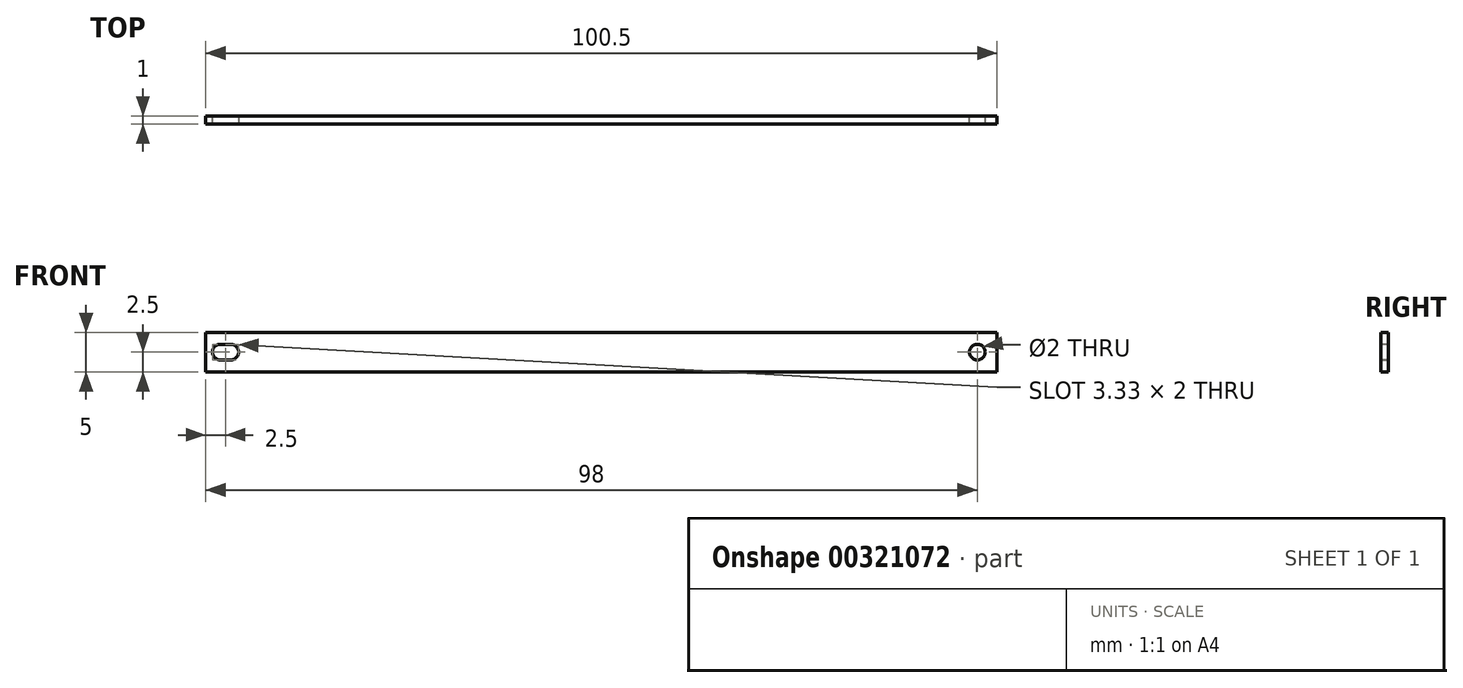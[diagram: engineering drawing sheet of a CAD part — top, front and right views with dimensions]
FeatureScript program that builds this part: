
annotation { "Feature Type Name" : "Feature", "Feature Type Description" : "" }
export const myFeature = defineFeature(function(context is Context, id is Id, definition is map)
    precondition{}
    {
        {
            var Q0;
            Q0=qCreatedBy(makeId("Front.planeOp"),FACE);
            var sketch = newSketch(context, id + "F0", { "sketchPlane" : qUnion([Q0])});
            skLineSegment(sketch, "E0.bottom", {"start": v(50.25, 2.5) * mm, "end": v(-50.25, 2.5) * mm});
            skLineSegment(sketch, "E0.top", {"start": v(50.25, -2.5) * mm, "end": v(-50.25, -2.5) * mm});
            skLineSegment(sketch, "E0.left", {"start": v(50.25, 2.5) * mm, "end": v(50.25, -2.5) * mm});
            skLineSegment(sketch, "E0.right", {"start": v(-50.25, 2.5) * mm, "end": v(-50.25, -2.5) * mm});
            skPoint(sketch, "E0.middle", {"position": v(0, 0) * mm});
            skCircle(sketch, "E1", {"center": v(47.75, 0) * mm, "radius": 1 * mm});
            skCircle(sketch, "E2", {"center": v(-47.75, 0) * mm, "radius": 1 * mm});
            skSolve(sketch);
        }
        {
            var Q0;
            Q0 = qSketchRegion(id + "F0", true);
            extrude(context, id + "F1", {"entities" : qUnion([Q0]), "depth" : 1 * mm});
        }
        {
            var Q0;
            Q0=makeQuery(id+"F1.opExtrude","CAP_FACE",FACE,{"disambiguationData":[OSD([sQuery(id+"F0.wireOp",EDGE,"E0.bottom"),sQuery(id+"F0.wireOp",EDGE,"E0.top"),sQuery(id+"F0.wireOp",EDGE,"E0.left"),sQuery(id+"F0.wireOp",EDGE,"E0.right"),sQuery(id+"F0.wireOp",EDGE,"E1"),sQuery(id+"F0.wireOp",EDGE,"E2")])],"isStart":false});
            var sketch = newSketch(context, id + "F2", { "sketchPlane" : qUnion([Q0])});
            skLineSegment(sketch, "E3.bottom", {"start": v(-46.09, 1) * mm, "end": v(-49.41, 1) * mm});
            skLineSegment(sketch, "E3.top", {"start": v(-46.09, -1) * mm, "end": v(-49.41, -1) * mm});
            skLineSegment(sketch, "E3.left", {"start": v(-46.09, 1) * mm, "end": v(-46.09, -1) * mm});
            skLineSegment(sketch, "E3.right", {"start": v(-49.41, 1) * mm, "end": v(-49.41, -1) * mm});
            skPoint(sketch, "E3.middle", {"position": v(-47.75, 0) * mm});
            skSolve(sketch);
        }
        {
            var Q0;
            Q0 = qSketchRegion(id + "F2", true);
            extrude(context, id + "F3", {"entities" : qUnion([Q0]), "operationType" : NewBodyOperationType.REMOVE, "oppositeDirection" : true, "depth" : 25 * mm});
        }
        {
            var Q0;
            Q0=makeQuery(id+"F3.boolean.opBoolean","COPY",EDGE,{"derivedFrom":makeQuery(id+"F3.opExtrude","SWEPT_EDGE",EDGE,{"disambiguationData":[OSD([sQuery(id+"F2.wireOp",EDGE,"E3.bottom"),sQuery(id+"F2.wireOp",EDGE,"E3.left")])]})});
            var Q1;
            Q1=makeQuery(id+"F3.boolean.opBoolean","COPY",EDGE,{"derivedFrom":makeQuery(id+"F3.opExtrude","SWEPT_EDGE",EDGE,{"disambiguationData":[OSD([sQuery(id+"F2.wireOp",EDGE,"E3.top"),sQuery(id+"F2.wireOp",EDGE,"E3.left")])]})});
            var Q2;
            Q2=makeQuery(id+"F3.boolean.opBoolean","COPY",EDGE,{"derivedFrom":makeQuery(id+"F3.opExtrude","SWEPT_EDGE",EDGE,{"disambiguationData":[OSD([sQuery(id+"F2.wireOp",EDGE,"E3.bottom"),sQuery(id+"F2.wireOp",EDGE,"E3.right")])]})});
            var Q3;
            Q3=makeQuery(id+"F3.boolean.opBoolean","COPY",EDGE,{"derivedFrom":makeQuery(id+"F3.opExtrude","SWEPT_EDGE",EDGE,{"disambiguationData":[OSD([sQuery(id+"F2.wireOp",EDGE,"E3.top"),sQuery(id+"F2.wireOp",EDGE,"E3.right")])]})});
            fillet(context, id + "F4", {"entities" : qUnion([Q0, Q1, Q2, Q3]), "radius" : 1 * mm, "tangentPropagation" : true, "allowEdgeOverflow" : false});
        }
    });
